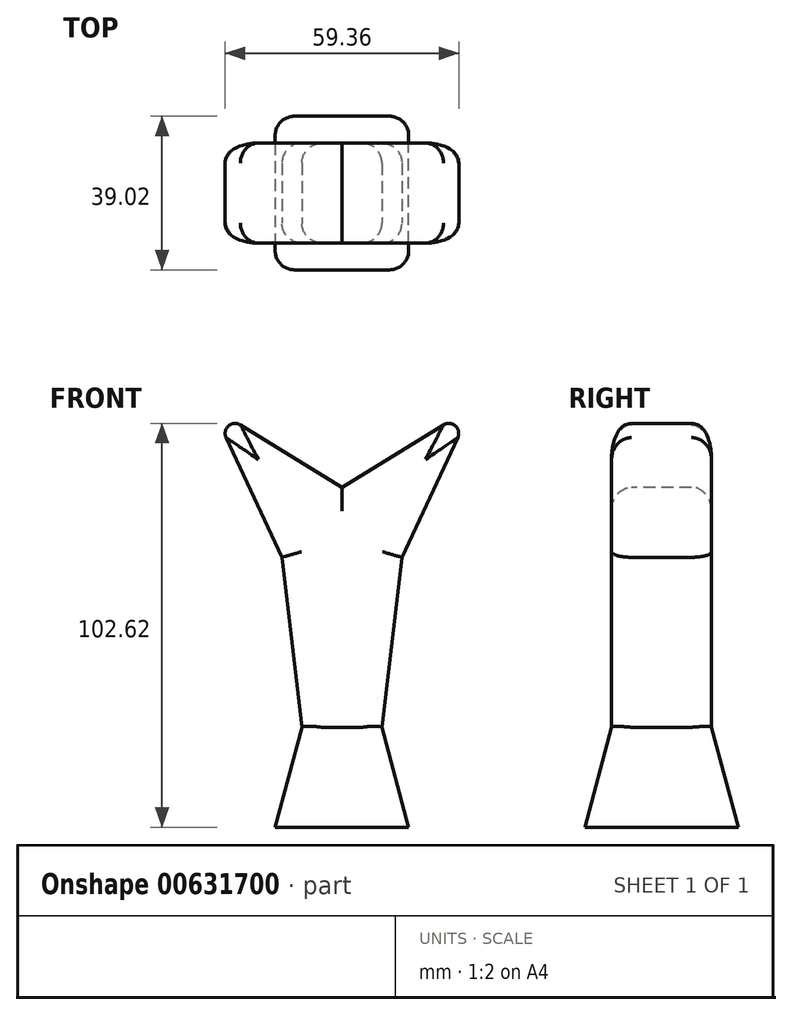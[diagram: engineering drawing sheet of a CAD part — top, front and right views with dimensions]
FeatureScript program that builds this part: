
annotation { "Feature Type Name" : "Feature", "Feature Type Description" : "" }
export const myFeature = defineFeature(function(context is Context, id is Id, definition is map)
    precondition{}
    {
        {
            var Q0;
            Q0=qCreatedBy(makeId("Front.planeOp"),FACE);
            var sketch = newSketch(context, id + "F0", { "sketchPlane" : qUnion([Q0])});
            skLineSegment(sketch, "E0", {"start": v(-33.02, 38.1) * mm, "end": v(-15.24, 0) * mm});
            skLineSegment(sketch, "E1", {"start": v(-15.24, 0) * mm, "end": v(-10.16, -43.18) * mm});
            skLineSegment(sketch, "E2", {"start": v(0, 17.78) * mm, "end": v(-33.02, 38.1) * mm});
            skLineSegment(sketch, "E3.MirrorCS", {"start": v(0, 17.78) * mm, "end": v(33.02, 38.1) * mm});
            skLineSegment(sketch, "E4.MirrorCS", {"start": v(33.02, 38.1) * mm, "end": v(15.24, 0) * mm});
            skLineSegment(sketch, "E5.MirrorCS", {"start": v(15.24, 0) * mm, "end": v(10.16, -43.18) * mm});
            skLineSegment(sketch, "E6", {"start": v(-10.16, -43.18) * mm, "end": v(10.16, -43.18) * mm});
            skSolve(sketch);
        }
        {
            var Q0;
            Q0=makeQuery(id+"F0.imprint","IMPRINT",FACE,{"disambiguationData":[TD([[makeQuery(id+"F0.imprint","IMPRINT",EDGE,{"derivedFrom":sQuery(id+"F0.wireOp",EDGE,"E0")}),1.0]])]});
            extrude(context, id + "F1", {"entities" : qUnion([Q0]), "oppositeDirection" : true, "depth" : 25.4 * mm, "offsetDistance" : 25.4 * mm});
        }
        {
            var Q0;
            Q0=makeQuery(id+"F1.opExtrude","SWEPT_FACE",FACE,{"disambiguationData":[OSD([sQuery(id+"F0.wireOp",EDGE,"2nTrqnA6-xQvH-oUp9-RFGd-O3IIfsPTzdWg")])]});
            var Q1;
            Q1=makeQuery(id+"F1.opExtrude","SWEPT_FACE",FACE,{"disambiguationData":[OSD([sQuery(id+"F0.wireOp",EDGE,"E6")])]});
            extrude(context, id + "F2", {"entities" : qUnion([Q0, Q1]), "operationType" : NewBodyOperationType.ADD, "depth" : 25.4 * mm, "offsetDistance" : 25.4 * mm, "hasDraft" : true, "draftAngle" : 15 * degree});
        }
        {
            var Q0;
            Q0=makeQuery(id+"F1.opExtrude","CAP_EDGE",EDGE,{"disambiguationData":[OSD([sQuery(id+"F0.wireOp",EDGE,"E2")])],"isStart":true});
            var Q1;
            Q1=makeQuery(id+"F1.opExtrude","CAP_EDGE",EDGE,{"disambiguationData":[OSD([sQuery(id+"F0.wireOp",EDGE,"E3.MirrorCS")])],"isStart":true});
            var Q2;
            Q2=makeQuery(id+"F1.opExtrude","CAP_EDGE",EDGE,{"disambiguationData":[OSD([sQuery(id+"F0.wireOp",EDGE,"E4.MirrorCS")])],"isStart":true});
            var Q3;
            Q3=makeQuery(id+"F1.opExtrude","CAP_EDGE",EDGE,{"disambiguationData":[OSD([sQuery(id+"F0.wireOp",EDGE,"E5.MirrorCS")])],"isStart":true});
            var Q4;
            {var subQ0=sQuery(id+"F0.wireOp",EDGE,"E6");var subQ1=sQuery(id+"F0.wireOp",EDGE,"E5.MirrorCS");Q4=makeQuery(id+"F2.opExtrude","SWEPT_EDGE",EDGE,{"disambiguationData":[OSD([subQ1,subQ0]),TDD([makeQuery(id+"F1.opExtrude","CAP_VERTEX",VERTEX,{"disambiguationData":[OSD([subQ1,subQ0])],"isStart":true})])]});}
            var Q5;
            {var subQ0=sQuery(id+"F0.wireOp",EDGE,"E6");var subQ1=sQuery(id+"F0.wireOp",EDGE,"E1");Q5=makeQuery(id+"F2.opExtrude","SWEPT_EDGE",EDGE,{"disambiguationData":[OSD([subQ1,subQ0]),TDD([makeQuery(id+"F1.opExtrude","CAP_VERTEX",VERTEX,{"disambiguationData":[OSD([subQ1,subQ0])],"isStart":true})])]});}
            var Q6;
            Q6=makeQuery(id+"F1.opExtrude","CAP_EDGE",EDGE,{"disambiguationData":[OSD([sQuery(id+"F0.wireOp",EDGE,"E1")])],"isStart":true});
            var Q7;
            Q7=makeQuery(id+"F1.opExtrude","CAP_EDGE",EDGE,{"disambiguationData":[OSD([sQuery(id+"F0.wireOp",EDGE,"E0")])],"isStart":true});
            var Q8;
            {var subQ0=sQuery(id+"F0.wireOp",EDGE,"E6");var subQ1=sQuery(id+"F0.wireOp",EDGE,"E1");Q8=makeQuery(id+"F2.opExtrude","SWEPT_EDGE",EDGE,{"disambiguationData":[OSD([subQ1,subQ0]),TDD([makeQuery(id+"F1.opExtrude","CAP_VERTEX",VERTEX,{"disambiguationData":[OSD([subQ1,subQ0])],"isStart":false})])]});}
            var Q9;
            Q9=makeQuery(id+"F1.opExtrude","CAP_EDGE",EDGE,{"disambiguationData":[OSD([sQuery(id+"F0.wireOp",EDGE,"E1")])],"isStart":false});
            var Q10;
            Q10=makeQuery(id+"F1.opExtrude","CAP_EDGE",EDGE,{"disambiguationData":[OSD([sQuery(id+"F0.wireOp",EDGE,"E0")])],"isStart":false});
            var Q11;
            Q11=makeQuery(id+"F1.opExtrude","CAP_EDGE",EDGE,{"disambiguationData":[OSD([sQuery(id+"F0.wireOp",EDGE,"E2")])],"isStart":false});
            var Q12;
            Q12=makeQuery(id+"F1.opExtrude","CAP_EDGE",EDGE,{"disambiguationData":[OSD([sQuery(id+"F0.wireOp",EDGE,"E3.MirrorCS")])],"isStart":false});
            var Q13;
            Q13=makeQuery(id+"F1.opExtrude","CAP_EDGE",EDGE,{"disambiguationData":[OSD([sQuery(id+"F0.wireOp",EDGE,"E4.MirrorCS")])],"isStart":false});
            var Q14;
            Q14=makeQuery(id+"F1.opExtrude","CAP_EDGE",EDGE,{"disambiguationData":[OSD([sQuery(id+"F0.wireOp",EDGE,"E5.MirrorCS")])],"isStart":false});
            var Q15;
            {var subQ0=sQuery(id+"F0.wireOp",EDGE,"E6");var subQ1=sQuery(id+"F0.wireOp",EDGE,"E5.MirrorCS");Q15=makeQuery(id+"F2.opExtrude","SWEPT_EDGE",EDGE,{"disambiguationData":[OSD([subQ1,subQ0]),TDD([makeQuery(id+"F1.opExtrude","CAP_VERTEX",VERTEX,{"disambiguationData":[OSD([subQ1,subQ0])],"isStart":false})])]});}
            fillet(context, id + "F3", {"entities" : qUnion([Q0, Q1, Q2, Q3, Q4, Q5, Q6, Q7, Q8, Q9, Q10, Q11, Q12, Q13, Q14, Q15]), "tangentPropagation" : true, "radius" : 5.08 * mm, "defaultsChanged" : false, "vertexSettings" : [], "allowEdgeOverflow" : false});
        }
        {
            var Q0;
            Q0=makeQuery(id+"F1.opExtrude","SWEPT_EDGE",EDGE,{"disambiguationData":[OSD([sQuery(id+"F0.wireOp",EDGE,"E3.MirrorCS"),sQuery(id+"F0.wireOp",EDGE,"E4.MirrorCS")])]});
            var Q1;
            Q1=makeQuery(id+"F1.opExtrude","SWEPT_EDGE",EDGE,{"disambiguationData":[OSD([sQuery(id+"F0.wireOp",EDGE,"E0"),sQuery(id+"F0.wireOp",EDGE,"E2")])]});
            fillet(context, id + "F4", {"entities" : qUnion([Q0, Q1]), "tangentPropagation" : true, "radius" : 2.54 * mm, "defaultsChanged" : true, "vertexSettings" : [], "allowEdgeOverflow" : false});
        }
    });
